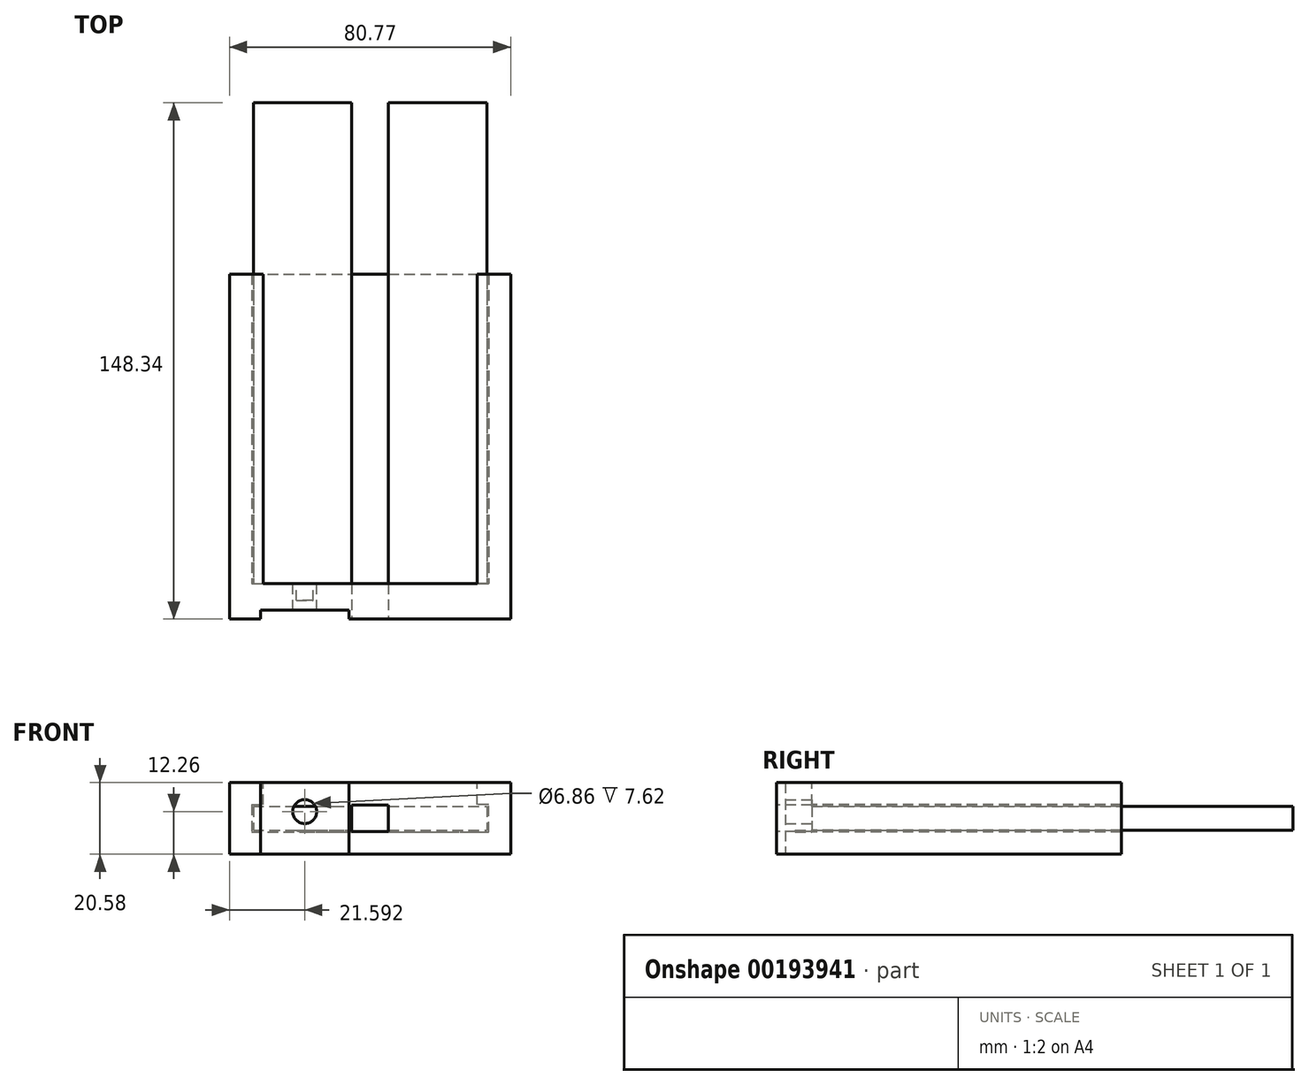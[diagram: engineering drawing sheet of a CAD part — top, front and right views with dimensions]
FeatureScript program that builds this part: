
annotation { "Feature Type Name" : "Feature", "Feature Type Description" : "" }
export const myFeature = defineFeature(function(context is Context, id is Id, definition is map)
    precondition{}
    {
        {
            var Q0;
            Q0=qCreatedBy(makeId("Front.planeOp"),FACE);
            var sketch = newSketch(context, id + "F0", { "sketchPlane" : qUnion([Q0])});
            skLineSegment(sketch, "E0", {"start": v(0, 0) * mm, "end": v(67.06, 0) * mm});
            skLineSegment(sketch, "E1", {"start": v(0, 0) * mm, "end": v(0, -6.86) * mm});
            skLineSegment(sketch, "E2", {"start": v(0, -6.86) * mm, "end": v(0, -6.86) * mm});
            skLineSegment(sketch, "E3", {"start": v(0, -6.86) * mm, "end": v(67.06, -6.86) * mm});
            skLineSegment(sketch, "E4", {"start": v(67.06, -6.86) * mm, "end": v(67.06, -6.86) * mm});
            skLineSegment(sketch, "E5", {"start": v(67.06, 0) * mm, "end": v(67.06, -6.86) * mm});
            skSolve(sketch);
        }
        {
            var Q0;
            Q0=makeQuery(id+"F0.imprint","IMPRINT",FACE,{"disambiguationData":[TD([[makeQuery(id+"F0.imprint","IMPRINT",EDGE,{"derivedFrom":sQuery(id+"F0.wireOp",EDGE,"E0")}),-1.0]])]});
            extrude(context, id + "F1", {"entities" : qUnion([Q0]), "oppositeDirection" : true, "depth" : 138.18 * mm});
        }
        {
            var Q0;
            Q0=makeQuery(id+"F1.opExtrude","CAP_FACE",FACE,{"disambiguationData":[OSD([sQuery(id+"F0.wireOp",EDGE,"E0"),sQuery(id+"F0.wireOp",EDGE,"E1"),sQuery(id+"F0.wireOp",EDGE,"E3"),sQuery(id+"F0.wireOp",EDGE,"E5")])],"isStart":true});
            var sketch = newSketch(context, id + "F2", { "sketchPlane" : qUnion([Q0])});
            skLineSegment(sketch, "E6", {"start": v(-0.5, 0) * mm, "end": v(-0.5, -7.37) * mm});
            skLineSegment(sketch, "E7", {"start": v(-0.5, -7.37) * mm, "end": v(67.56, -7.37) * mm});
            skLineSegment(sketch, "E8", {"start": v(67.56, -7.37) * mm, "end": v(67.56, 0) * mm});
            skLineSegment(sketch, "E9", {"start": v(-6.86, 6.86) * mm, "end": v(-6.86, -13.72) * mm});
            skLineSegment(sketch, "E10", {"start": v(-6.86, -13.72) * mm, "end": v(73.91, -13.72) * mm});
            skLineSegment(sketch, "E11", {"start": v(73.91, 6.86) * mm, "end": v(73.91, -13.72) * mm});
            skLineSegment(sketch, "E12", {"start": v(67.56, 0) * mm, "end": v(67.56, 0.5) * mm});
            skLineSegment(sketch, "E13", {"start": v(67.56, 0.5) * mm, "end": v(64.26, 0.5) * mm});
            skLineSegment(sketch, "E14", {"start": v(64.26, 0.5) * mm, "end": v(64.26, 6.86) * mm});
            skLineSegment(sketch, "E15", {"start": v(64.26, 6.86) * mm, "end": v(73.91, 6.86) * mm});
            skLineSegment(sketch, "E16", {"start": v(-0.5, 0) * mm, "end": v(-0.5, 0.5) * mm});
            skLineSegment(sketch, "E17", {"start": v(-0.5, 0.5) * mm, "end": v(2.8, 0.5) * mm});
            skLineSegment(sketch, "E18", {"start": v(2.8, 0.5) * mm, "end": v(2.8, 6.86) * mm});
            skLineSegment(sketch, "E19", {"start": v(2.8, 6.86) * mm, "end": v(-6.86, 6.86) * mm});
            skSolve(sketch);
        }
        {
            var Q0;
            Q0=makeQuery(id+"F2.imprint","IMPRINT",FACE,{"disambiguationData":[TD([[makeQuery(id+"F2.imprint","IMPRINT",EDGE,{"derivedFrom":sQuery(id+"F2.wireOp",EDGE,"E6")}),-1.0]])]});
            extrude(context, id + "F3", {"entities" : qUnion([Q0]), "oppositeDirection" : true, "depth" : 88.9 * mm});
        }
        {
            var Q0;
            Q0=qCreatedBy(makeId("Right.planeOp"),FACE);
            var sketch = newSketch(context, id + "F4", { "sketchPlane" : qUnion([Q0])});
            skLineSegment(sketch, "E20.bottom", {"start": v(0, 6.86) * mm, "end": v(-10.16, 6.86) * mm});
            skLineSegment(sketch, "E20.top", {"start": v(0, -13.72) * mm, "end": v(-10.16, -13.72) * mm});
            skLineSegment(sketch, "E20.left", {"start": v(0, 6.86) * mm, "end": v(0, -13.72) * mm});
            skLineSegment(sketch, "E20.right", {"start": v(-10.16, 6.86) * mm, "end": v(-10.16, -13.72) * mm});
            skSolve(sketch);
        }
        {
            var Q0;
            Q0=makeQuery(id+"F4.imprint","IMPRINT",FACE,{"disambiguationData":[TD([[makeQuery(id+"F4.imprint","IMPRINT",EDGE,{"derivedFrom":sQuery(id+"F4.wireOp",EDGE,"E20.bottom")}),1.0]])]});
            var Q1;
            Q1=makeQuery(id+"F3.opExtrude","CAP_VERTEX",VERTEX,{"disambiguationData":[OSD([sQuery(id+"F2.wireOp",EDGE,"E11"),sQuery(id+"F2.wireOp",EDGE,"E15")])],"isStart":true});
            var Q2;
            Q2=makeQuery(id+"F3.opExtrude","CAP_VERTEX",VERTEX,{"disambiguationData":[OSD([sQuery(id+"F2.wireOp",EDGE,"E9"),sQuery(id+"F2.wireOp",EDGE,"E19")])],"isStart":true});
            extrude(context, id + "F5", {"entities" : qUnion([Q0]), "operationType" : NewBodyOperationType.ADD, "endBound" : BoundingType.UP_TO_VERTEX, "endBoundEntityVertex" : qUnion([Q1]), "depth" : 25.4 * mm, "hasSecondDirection" : true, "secondDirectionBound" : SecondDirectionBoundingType.UP_TO_VERTEX, "secondDirectionOppositeDirection" : true, "secondDirectionBoundEntityVertex" : qUnion([Q2]), "secondDirectionDepth" : 25.4 * mm});
        }
        {
            var Q0;
            Q0=makeQuery(id+"F5.opExtrude","SWEPT_FACE",FACE,{"disambiguationData":[OSD([sQuery(id+"F4.wireOp",EDGE,"E20.right")])]});
            var sketch = newSketch(context, id + "F6", { "sketchPlane" : qUnion([Q0])});
            skLineSegment(sketch, "E21.bottom", {"start": v(38.8, 0.38) * mm, "end": v(28.26, 0.38) * mm});
            skLineSegment(sketch, "E21.top", {"start": v(38.8, -7.24) * mm, "end": v(28.26, -7.24) * mm});
            skLineSegment(sketch, "E21.left", {"start": v(38.8, 0.38) * mm, "end": v(38.8, -7.24) * mm});
            skLineSegment(sketch, "E21.right", {"start": v(28.26, 0.38) * mm, "end": v(28.26, -7.24) * mm});
            skPoint(sketch, "E21.middle", {"position": v(33.53, -3.43) * mm});
            skPoint(sketch, "E21.middle.positionSnap0", {"position": v(33.53, 6.86) * mm});
            skPoint(sketch, "E21.middle.positionSnap1", {"position": v(73.91, -3.43) * mm});
            skPoint(sketch, "E21.centerSnap0", {"position": v(33.53, 6.86) * mm});
            skPoint(sketch, "E21.centerSnap1", {"position": v(73.91, -3.43) * mm});
            skSolve(sketch);
        }
        {
            var Q0;
            Q0=makeQuery(id+"F6.imprint","IMPRINT",FACE,{"disambiguationData":[TD([[makeQuery(id+"F6.imprint","IMPRINT",EDGE,{"derivedFrom":sQuery(id+"F6.wireOp",EDGE,"E21.bottom")}),1.0]])]});
            extrude(context, id + "F7", {"entities" : qUnion([Q0]), "operationType" : NewBodyOperationType.REMOVE, "endBound" : BoundingType.THROUGH_ALL, "oppositeDirection" : true, "depth" : 25.4 * mm});
        }
        {
            var Q0;
            Q0=makeQuery(id+"F5.opExtrude","SWEPT_FACE",FACE,{"disambiguationData":[OSD([sQuery(id+"F4.wireOp",EDGE,"E20.left")])]});
            var sketch = newSketch(context, id + "F8", { "sketchPlane" : qUnion([Q0])});
            skPoint(sketch, "E22", {"position": v(0.5, -3.43) * mm});
            skCircle(sketch, "E23", {"center": v(-14.73, -1.46) * mm, "radius": 5.9 * mm});
            skCircle(sketch, "E24", {"center": v(-14.73, -1.46) * mm, "radius": 3.43 * mm});
            skSolve(sketch);
        }
        {
            var Q0;
            Q0=makeQuery(id+"F8.imprint","IMPRINT",FACE,{"disambiguationData":[TD([[makeQuery(id+"F8.imprint","IMPRINT",EDGE,{"derivedFrom":sQuery(id+"F8.wireOp",EDGE,"E24")}),1.0]])]});
            extrude(context, id + "F9", {"entities" : qUnion([Q0]), "operationType" : NewBodyOperationType.REMOVE, "endBound" : BoundingType.THROUGH_ALL, "oppositeDirection" : true, "depth" : 25.4 * mm});
        }
        {
            var Q0;
            Q0=makeQuery(id+"F8.imprint","IMPRINT",FACE,{"disambiguationData":[TD([[makeQuery(id+"F8.imprint","IMPRINT",EDGE,{"derivedFrom":sQuery(id+"F8.wireOp",EDGE,"E23")}),1.0]])]});
            extrude(context, id + "F10", {"entities" : qUnion([Q0]), "operationType" : NewBodyOperationType.REMOVE, "oppositeDirection" : true, "depth" : 4.83 * mm});
        }
        {
            var Q0;
            Q0=makeQuery(id+"F5.opExtrude","SWEPT_FACE",FACE,{"disambiguationData":[OSD([sQuery(id+"F4.wireOp",EDGE,"E20.right")])]});
            var sketch = newSketch(context, id + "F11", { "sketchPlane" : qUnion([Q0])});
            skLineSegment(sketch, "E25", {"start": v(14.73, -1.46) * mm, "end": v(14.73, -13.72) * mm, "construction": true});
            skLineSegment(sketch, "E26", {"start": v(27.43, 6.86) * mm, "end": v(27.43, -13.72) * mm});
            skLineSegment(sketch, "E27", {"start": v(2.03, 6.86) * mm, "end": v(2.03, -13.72) * mm});
            skLineSegment(sketch, "E28", {"start": v(2.03, 6.86) * mm, "end": v(27.43, 6.86) * mm});
            skLineSegment(sketch, "E29", {"start": v(2.03, -13.72) * mm, "end": v(27.43, -13.72) * mm});
            skSolve(sketch);
        }
        {
            var Q0;
            Q0=makeQuery(id+"F11.imprint","IMPRINT",FACE,{"disambiguationData":[TD([[makeQuery(id+"F11.imprint","IMPRINT",EDGE,{"derivedFrom":sQuery(id+"F11.wireOp",EDGE,"E26")}),-1.0]])]});
            extrude(context, id + "F12", {"entities" : qUnion([Q0]), "operationType" : NewBodyOperationType.REMOVE, "oppositeDirection" : true, "depth" : 2.54 * mm});
        }
    });
